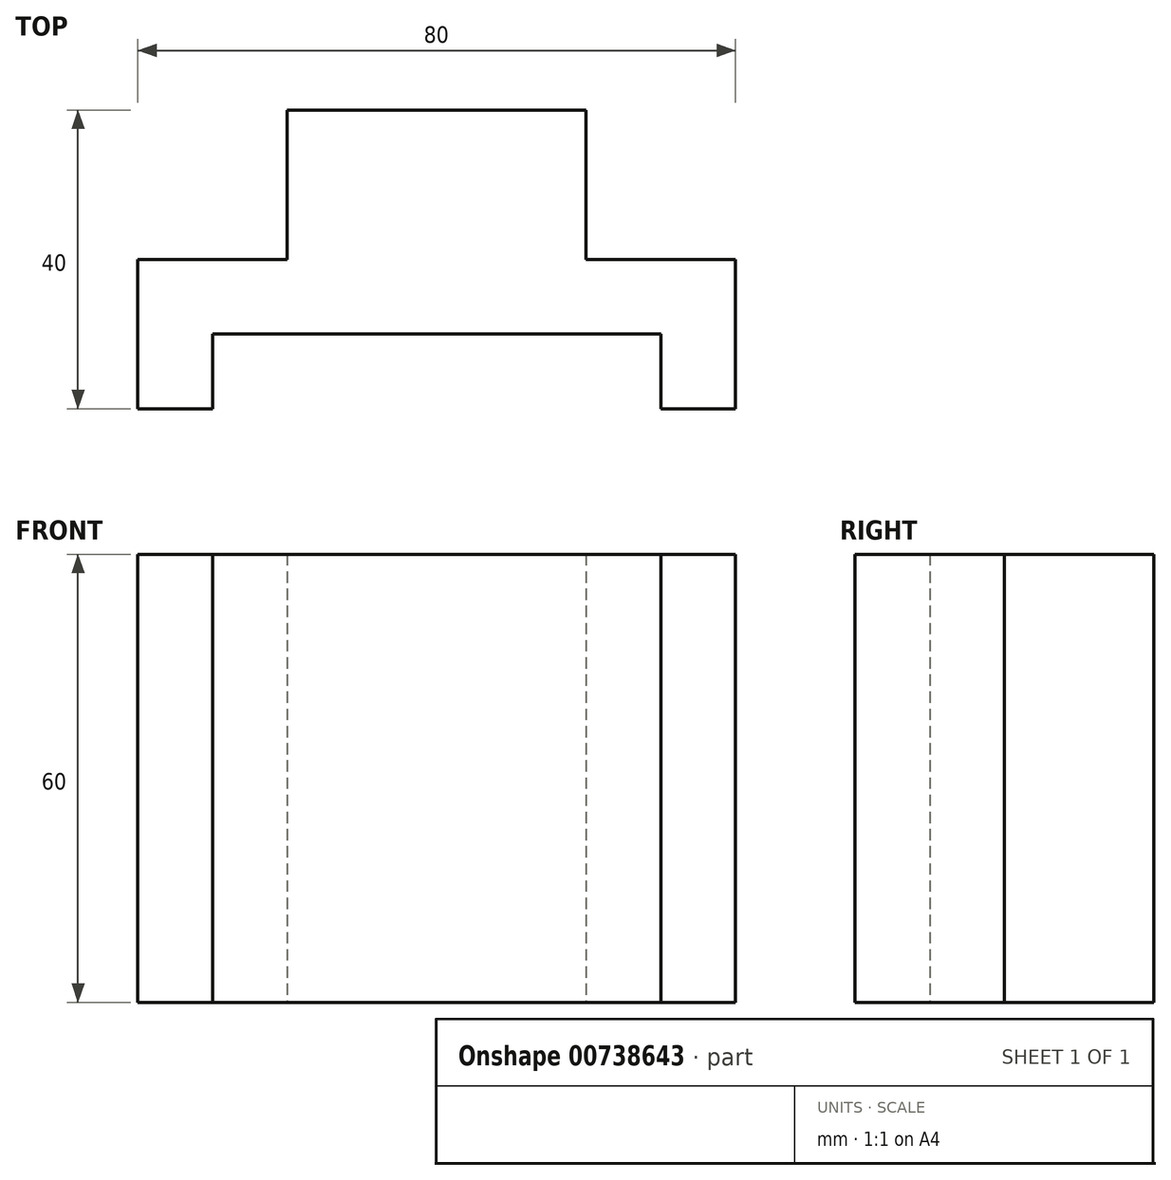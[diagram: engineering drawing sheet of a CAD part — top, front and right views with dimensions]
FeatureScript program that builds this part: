
annotation { "Feature Type Name" : "Feature", "Feature Type Description" : "" }
export const myFeature = defineFeature(function(context is Context, id is Id, definition is map)
    precondition{}
    {
        {
            var Q0;
            Q0=qCreatedBy(makeId("Front.planeOp"),FACE);
            var sketch = newSketch(context, id + "F0", { "sketchPlane" : qUnion([Q0])});
            skLineSegment(sketch, "E0.bottom", {"start": v(-36.03, 13.46) * mm, "end": v(43.97, 13.46) * mm});
            skLineSegment(sketch, "E0.top", {"start": v(-36.03, -46.54) * mm, "end": v(43.97, -46.54) * mm});
            skLineSegment(sketch, "E0.left", {"start": v(-36.03, 13.46) * mm, "end": v(-36.03, -46.54) * mm});
            skLineSegment(sketch, "E0.right", {"start": v(43.97, 13.46) * mm, "end": v(43.97, -46.54) * mm});
            skSolve(sketch);
        }
        {
            var Q0;
            Q0=makeQuery(id+"F0.imprint","IMPRINT",FACE,{"disambiguationData":[TD([[makeQuery(id+"F0.imprint","IMPRINT",EDGE,{"derivedFrom":sQuery(id+"F0.wireOp",EDGE,"E0.bottom")}),-1.0]])]});
            extrude(context, id + "F1", {"entities" : qUnion([Q0]), "depth" : 40 * mm, "offsetDistance" : 25 * mm});
        }
        {
            var Q0;
            Q0=makeQuery(id+"F1.opExtrude","CAP_FACE",FACE,{"disambiguationData":[OSD([sQuery(id+"F0.wireOp",EDGE,"E0.bottom"),sQuery(id+"F0.wireOp",EDGE,"E0.top"),sQuery(id+"F0.wireOp",EDGE,"E0.left"),sQuery(id+"F0.wireOp",EDGE,"E0.right")])],"isStart":false});
            var sketch = newSketch(context, id + "F2", { "sketchPlane" : qUnion([Q0])});
            skLineSegment(sketch, "E1.bottom", {"start": v(-36.03, 13.46) * mm, "end": v(-26.03, 13.46) * mm});
            skLineSegment(sketch, "E1.top", {"start": v(-36.03, -46.54) * mm, "end": v(-26.03, -46.54) * mm});
            skLineSegment(sketch, "E1.left", {"start": v(-36.03, 13.46) * mm, "end": v(-36.03, -46.54) * mm});
            skLineSegment(sketch, "E1.right", {"start": v(-26.03, 13.46) * mm, "end": v(-26.03, -46.54) * mm});
            skLineSegment(sketch, "E2.bottom", {"start": v(43.97, 13.46) * mm, "end": v(33.97, 13.46) * mm});
            skLineSegment(sketch, "E2.top", {"start": v(43.97, -46.54) * mm, "end": v(33.97, -46.54) * mm});
            skLineSegment(sketch, "E2.left", {"start": v(43.97, 13.46) * mm, "end": v(43.97, -46.54) * mm});
            skLineSegment(sketch, "E2.right", {"start": v(33.97, 13.46) * mm, "end": v(33.97, -46.54) * mm});
            skSolve(sketch);
        }
        {
            var Q0;
            {var subQ0=sQuery(id+"F2.wireOp",EDGE,"E1.right");Q0=makeQuery(id+"F2.imprint","IMPRINT",FACE,{"disambiguationData":[TD([[makeQuery(id+"F2.imprint","IMPRINT",EDGE,{"derivedFrom":subQ0}),1.0]])]});}
            extrude(context, id + "F3", {"entities" : qUnion([Q0]), "operationType" : NewBodyOperationType.REMOVE, "oppositeDirection" : true, "depth" : 10 * mm, "offsetDistance" : 25 * mm});
        }
        {
            var Q0;
            Q0=makeQuery(id+"F1.opExtrude","CAP_FACE",FACE,{"disambiguationData":[OSD([sQuery(id+"F0.wireOp",EDGE,"E0.bottom"),sQuery(id+"F0.wireOp",EDGE,"E0.top"),sQuery(id+"F0.wireOp",EDGE,"E0.left"),sQuery(id+"F0.wireOp",EDGE,"E0.right")])],"isStart":true});
            var sketch = newSketch(context, id + "F4", { "sketchPlane" : qUnion([Q0])});
            skLineSegment(sketch, "E3.bottom", {"start": v(-23.97, 13.46) * mm, "end": v(16.03, 13.46) * mm});
            skLineSegment(sketch, "E3.top", {"start": v(-23.97, -46.54) * mm, "end": v(16.03, -46.54) * mm});
            skLineSegment(sketch, "E3.left", {"start": v(-23.97, 13.46) * mm, "end": v(-23.97, -46.54) * mm});
            skLineSegment(sketch, "E3.right", {"start": v(16.03, 13.46) * mm, "end": v(16.03, -46.54) * mm});
            skSolve(sketch);
        }
        {
            var Q0;
            {var subQ0=sQuery(id+"F4.wireOp",EDGE,"E3.right");Q0=makeQuery(id+"F4.imprint","IMPRINT",FACE,{"disambiguationData":[TD([[makeQuery(id+"F4.imprint","IMPRINT",EDGE,{"derivedFrom":subQ0}),1.0]])]});}
            var Q1;
            {var subQ0=sQuery(id+"F4.wireOp",EDGE,"E3.left");Q1=makeQuery(id+"F4.imprint","IMPRINT",FACE,{"disambiguationData":[TD([[makeQuery(id+"F4.imprint","IMPRINT",EDGE,{"derivedFrom":subQ0}),-1.0]])]});}
            extrude(context, id + "F5", {"entities" : qUnion([Q0, Q1]), "operationType" : NewBodyOperationType.REMOVE, "oppositeDirection" : true, "depth" : 20 * mm, "offsetDistance" : 25 * mm});
        }
    });
